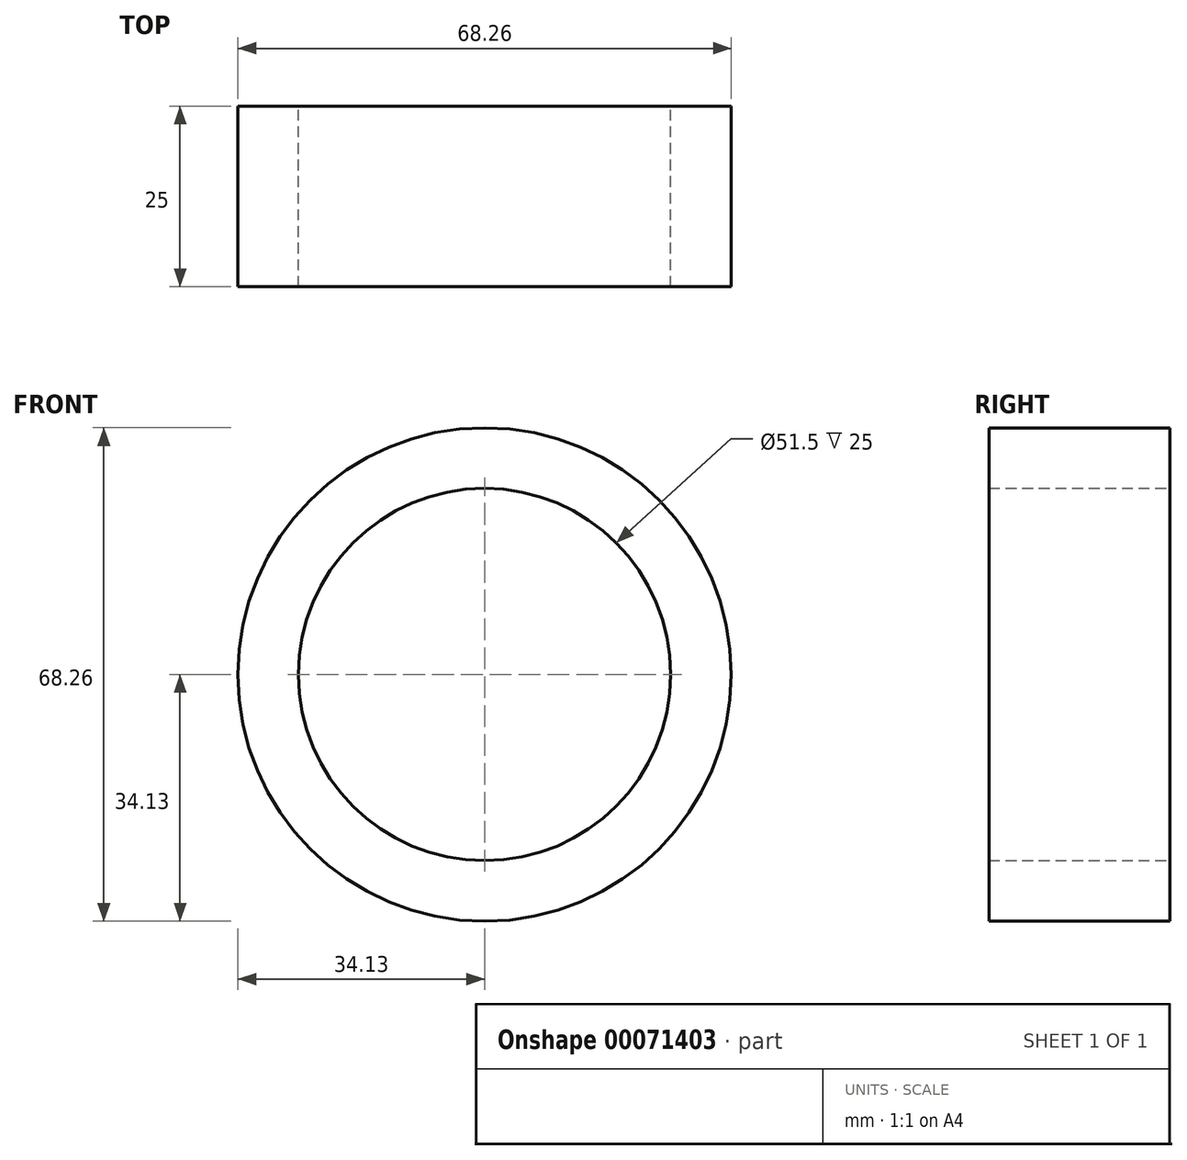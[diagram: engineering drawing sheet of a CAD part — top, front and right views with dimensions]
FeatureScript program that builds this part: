
annotation { "Feature Type Name" : "Feature", "Feature Type Description" : "" }
export const myFeature = defineFeature(function(context is Context, id is Id, definition is map)
    precondition{}
    {
        {
            var Q0;
            Q0=qCreatedBy(makeId("Front.planeOp"),FACE);
            var sketch = newSketch(context, id + "F0", { "sketchPlane" : qUnion([Q0])});
            skCircle(sketch, "E0", {"center": v(0, 0) * mm, "radius": 34.12 * mm});
            skCircle(sketch, "E1", {"center": v(0, 0) * mm, "radius": 25.75 * mm});
            skSolve(sketch);
        }
        {
            var Q0;
            Q0=makeQuery(id+"F0.imprint","IMPRINT",FACE,{"disambiguationData":[TD([[makeQuery(id+"F0.imprint","IMPRINT",EDGE,{"derivedFrom":sQuery(id+"F0.wireOp",EDGE,"E0")}),1.0]])]});
            extrude(context, id + "F1", {"entities" : qUnion([Q0]), "depth" : 25 * mm});
        }
    });
